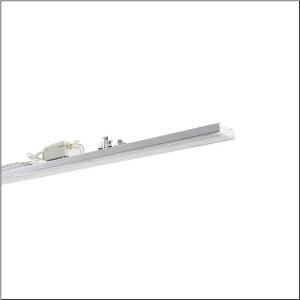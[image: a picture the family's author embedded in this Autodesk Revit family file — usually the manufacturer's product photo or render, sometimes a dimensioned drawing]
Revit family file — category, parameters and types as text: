
# Revit family: licross_r__11_recessed_ho_51tl18dv4m1m_dde3
name_source: partatom
category: Lighting Fixtures
units: mm (PartAtom-declared; Revit-internal decimal feet)

## family parameters
Cut with Voids When Loaded = No
Host = Face
Light Source = No
Part Type = Normal
Room Calculation Point = No
Round Connector Dimension = Use Diameter
Shared = No

## types (1)
- --- (1 x LED, 26860 lm, 150.5 W, 4000K)
    Apparent Load = 150 VA
    CIE Flux Codes = 78 94 99 100 100
    Color Rendering = 80
    Color Temperature = 4000K
    Default Elevation = 1800 mm
    Description = Licross® 11 Recessed HO, luminaire insert, of sheet steel, coil coated, white, length: 2.250mm, width: 66mm, height: 67mm, LED rated luminous flux: 26.870lm, light colour: 840, control gear: DALI 2, with plug, 5-pole, with phase selection, mains connection: 220..240V, AC, 50/60Hz, rated input power: 151W, halogen-free wiring, primary light control with lens, of plastic, primary optical cover: cover, of PMMA, light emission: direct distribution, primary light characteristic: symmetric, protection rating (complete): IP40, insulation class (complete): insulation class I (protective earthing), certification: CE, ENEC, VDE, UKCA, protection symbol: D if used in an environment without relevant dust loads with corresponding accessories, impact resistance: IK06, permissible ambient temperature for indoor applications: -40..+35°C, corresponds to IFS (International Featured Standards) requirements for safety and quality in the food industry, reducing of maximum allowable ambient temperature of 5°C with ceiling mounting, LABS conformity tested according to VDMA 24364:2018-05, packaging unit: 1 piece
    Height = 58 mm
    Lamp = 1 x LED
    Lamp Light Flux = 26860 lm
    Lamp Power = 150.5 W
    Lamp count = 1
    Length = 2250 mm
    Luminous efficacy = 178 lm/W
    Manufacturer = Siteco
    ModVariant = No
    Model = 51TL18DV4M1M
    Mounting Place = Ceiling
    Mounting Type = Pendant
    Number of Poles = 1
    OnlyDefault = Yes
    Power Factor = 1
    Product Name = Licross® 11 Recessed HO
    Product group = luminaire insert
    ProductGroupID = 901
    Protection Class = Protection class I
    Protection Degree = IP 40
    RLX_Detail_Level = 1
    RLX_Emergency_Light_Flux = 0 lm
    RLX_Emergency_Type = 0
    RLX_Emergency_Type_DB = No
    RlxData = <blob elided: 29785 chars, md5=8414c169>
    Socket = socket
    Standby Power = 0 W
    System Light Flux = 26860 lm
    System Power = 150 W
    Type Comments = factory setting: luminous flux: 100 % | dim-lin: 254 | 690 mA
    Type Image = l_1296930.jpg
    URL = http://relux.com
    VarID = @adj_094716
    Voltage = 0 V
    Weight = 0.00 kg
    Width = 66 mm

## geometry (parser evidence)
native form markers: Blend x4, Sweep x11
no freeform markers — native parametric forms only
